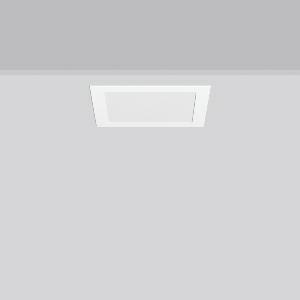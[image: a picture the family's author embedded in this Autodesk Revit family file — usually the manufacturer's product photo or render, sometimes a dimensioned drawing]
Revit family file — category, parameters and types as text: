
# Revit family: toledo_flat_square_e_901716_002_19_0598
name_source: partatom
category: Lighting Fixtures
units: mm (PartAtom-declared; Revit-internal decimal feet)

## family parameters
Cut with Voids When Loaded = No
Host = Face
Light Source = No
Part Type = Normal
Room Calculation Point = No
Round Connector Dimension = Use Diameter
Shared = No

## types (1)
- TOLEDO FLAT square E (1 x LED Modul 830, 1650 lm, 3000)
    Apparent Load = 17 VA
    CIE Flux Codes = 48 80 96 100 100
    Color Rendering = 80
    Color Temperature = 3000
    Default Elevation = 1800 mm
    Description = Series: TOLEDO FLAT square
Ultra thin recessed downlight. Housing: die-cast aluminium. Light guide and diffuser made of non-yellowing PMMA, opal matt. Ceiling installation with spring system. Mounting depth depends on ceiling strength. Including separate LED converter with connecting cable 250 mm.Connected HF motion detector in a separate ballast box.Adjustable dim functions Soft Start, Corridor, Permanent. Wireless networking, sensor configuration and communication via Bluetooth. Operation via an Android / iOS device, free app available for download. master/slave Brightness sensor without function. Not suitable for metal ceilings.Versions with movement sensor not suitable for surface-mounted housing. Suitable for through-wiring with separately available accessories. Retrofittable decorative cylinders made of chintz fabric as accessory, optional with satin finish plastic diffuser. Through-wiring box (5 pole) available as accessory. 
Colour: white
Length: 225 mm
Width: 225 mm
Height: 3 mm
Cut-out length: 208 mm
Cut-out width: 208 mm
Recess height: 55-76 mm
Luminaire: recess height: 31-51 mm
Lamp: LED
Socket: without socket
Colour temperature: 3000K
Colour rendering index (CRI): 80
System power: 17 W
Rated luminous flux: 1650 lm
Luminous efficiency: 97 lm/W
Control gear: Dimmable Bluetooth converter
Protection class: I
Type of protection: IP 54
    Height = 0 mm  [stored 0 ft]
    Lamp = 1 x LED Modul 830
    Lamp Light Flux = 1650 lm
    Lamp count = 1
    Length = 225 mm
    Lifetime = 50000 h
    Luminous efficacy = 97 lm/W
    Manufacturer = RZB
    ModVariant = No
    Model = 901716.002.19
    Mounting Place = Ceiling
    Mounting Type = Recessed
    Number of Poles = 1
    OnlyDefault = Yes
    Power Factor = 1
    Product Name = TOLEDO FLAT square E
    Product group = Recessed downlights
    ProductGroupID = 402
    Protection Class = Protection class I
    Protection Degree = IP 20
    RLX_Detail_Level = 1
    RLX_Emergency_Light_Flux = 0 lm
    RLX_Emergency_Type = 0
    RLX_Emergency_Type_DB = No
    RlxData = <blob elided: 11481 chars, md5=31aec0e4>
    Socket = socket
    Standby Power = 0 W
    System Light Flux = 1650 lm
    System Power = 17 W
    Type Comments = Product without accessories
    Type Image = 901487.002.jpg
    URL = http://relux.com
    VarID = ---
    Voltage = 230 V
    Voltage Range = 220-240 V
    Weight = 0.00 kg
    Width = 225 mm

note: [stored X ft] marks values corroborated as IEEE doubles in the binary element streams (Revit-internal decimal feet)

## geometry (parser evidence)
native form markers: Sweep x11
no freeform markers — native parametric forms only
